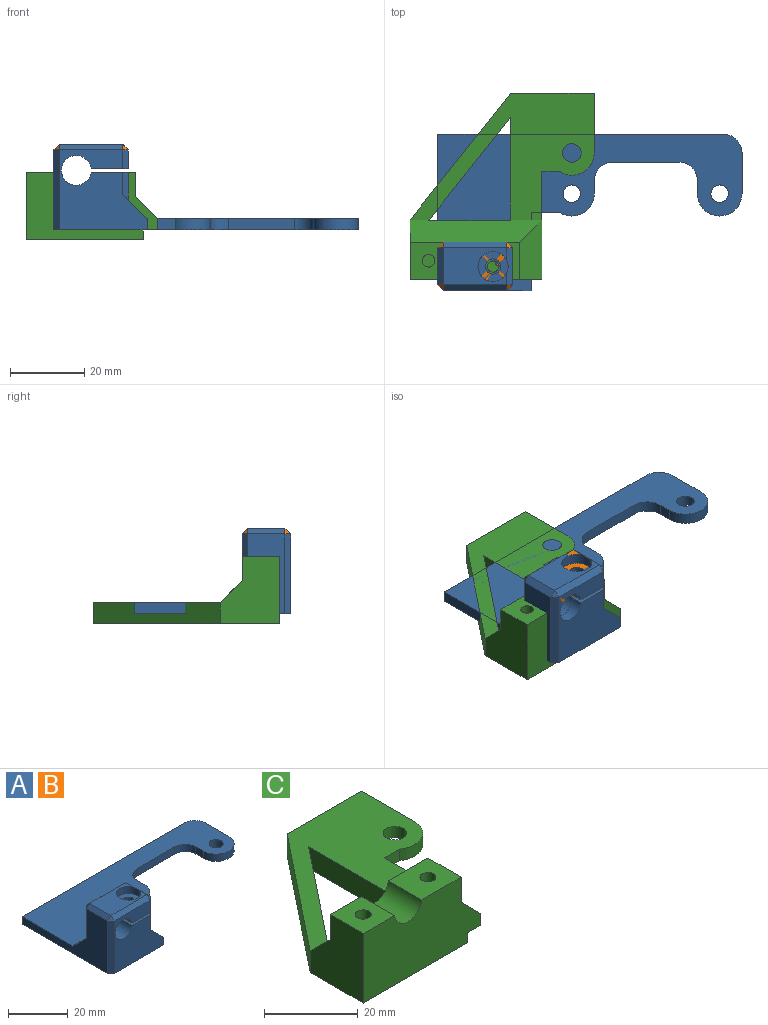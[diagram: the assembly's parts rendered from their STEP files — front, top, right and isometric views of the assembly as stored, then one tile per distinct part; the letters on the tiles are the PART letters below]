
ASSEMBLY  parts=3 mates=1
PART A: 46 faces, bbox 81.8x42x23 mm
  f0: plane 23.53x21.5mm, normal (0,-1,0), area 347.4mm2, adj f16,f18,f19,f22,f24,f25,f26,f37
  f1: plane 10x5mm, normal (1,0,0), area 50mm2, adj f25,f31,f36,f37
  f2: plane 10x7.5mm, normal (1,0,0), area 75mm2, adj f22,f26,f43,f44
  f3: plane 7.56x3mm, normal (0,-1,0), area 22.7mm2, adj f4,f16,f18,f19
  f4: cylinder r=6mm len=9.41mm, axis (0,0,-1), area 39.2mm2, adj f3,f5,f18,f19
  f5: plane 3.5x3mm, normal (1,0,0), area 10.5mm2, adj f4,f6,f18,f19
  f6: cylinder r=5mm len=5mm, axis (0,0,-1), area 23.6mm2, adj f5,f7,f18,f19
  f7: plane 17.75x3mm, normal (0,-1,0), area 53.2mm2, adj f6,f8,f18,f19
  f8: cylinder r=5mm len=5mm, axis (0,0,-1), area 23.6mm2, adj f7,f9,f18,f19
  f9: plane 3.5x3mm, normal (-1,0,0), area 10.5mm2, adj f8,f10,f18,f19
  f10: cylinder r=6mm len=12mm, axis (0,0,-1), area 56.5mm2, adj f9,f11,f18,f19
  f11: plane 11x3mm, normal (1,0,0), area 33mm2, adj f10,f12,f18,f19
  f12: cylinder r=5mm len=5mm, axis (0,0,-1), area 23.6mm2, adj f11,f13,f18,f19
  f13: plane 76.75x3mm, normal (0,1,0), area 230.3mm2, adj f12,f14,f18,f19
  f14: plane 40.54x21.5mm, normal (-1,0,0), area 327.7mm2, adj f13,f18,f19,f23,f32,f38,f39
  f15: cylinder r=2.35mm len=4.7mm, axis (0,0,-1), area 44.3mm2, adj f18,f19
  f16: plane 21.11x3mm, normal (1,0,0), area 63.3mm2, adj f0,f3,f18,f19
  f17: cylinder r=2.35mm len=4.7mm, axis (0,0,-1), area 44.3mm2, adj f18,f19
  f18: plane 81.75x42.04mm, normal (0,0,1), area 1385.9mm2, adj f0,f3,f4,f5,f6,f7,f8,f9
  f19: plane 81.75x42.04mm, normal (0,0,-1), area 1834.8mm2, adj f0,f3,f4,f5,f6,f7,f8,f9
  f20: plane 17x13.5mm, normal (0,1,0), area 170.7mm2, adj f23,f24,f25,f26,f31,f32,f33,f44
  f21: plane 17x10mm, normal (0,0,1), area 119.3mm2, adj f27,f33,f36,f39,f42
  f22: plane 18x6.5mm, normal (0.71,0,0.71), area 112mm2, adj f0,f2,f18,f23,f43,f44
  f23: plane 25x6.5mm, normal (0,0.71,0.71), area 161.5mm2, adj f14,f18,f20,f22,f32,f44
  f24: cylinder r=4mm len=13mm, axis (0,1,0), area 313.7mm2, adj f0,f20,f25,f26
  f25: plane 13x10.03mm, normal (0,0,-1), area 115mm2, adj f0,f1,f20,f24,f31,f37,f45
  f26: plane 13x10.03mm, normal (0,0,1), area 121.1mm2, adj f0,f2,f20,f24,f29,f43,f44
  f27: cylinder r=4.05mm len=8.1mm, axis (0,0,1), area 75.5mm2, adj f21,f28,f36
  f28: plane 8.1x8.1mm, normal (0,0,1), area 38.3mm2, adj f27,f45
  f29: cylinder r=1.5mm len=5.5mm, axis (0,0,1), area 51.8mm2, adj f26,f30
  f30: plane 3x3mm, normal (0,0,1), area 7.1mm2, adj f29
  f31: plane 5x1.5mm, normal (0.71,0.71,0), area 10.6mm2, adj f1,f20,f25,f34
  f32: plane 13.5x1.5mm, normal (-0.71,0.71,0), area 27mm2, adj f14,f20,f23,f35
  f33: plane 17x1.5mm, normal (0,0.71,0.71), area 36.1mm2, adj f20,f21,f34,f35
  f34: plane 1.5x1.5mm, normal (0.58,0.58,0.58), area 1.9mm2, adj f31,f33,f36
  f35: plane 1.5x1.5mm, normal (-0.58,0.58,0.58), area 1.9mm2, adj f32,f33,f39
  f36: plane 10x1.5mm, normal (0.71,0,0.71), area 20.1mm2, adj f1,f21,f27,f34,f40
  f37: plane 5x1.5mm, normal (0.71,-0.71,0), area 10.6mm2, adj f0,f1,f25,f40
  f38: plane 21.5x1.5mm, normal (-0.71,-0.71,0), area 45.6mm2, adj f0,f14,f19,f41
  f39: plane 10x1.5mm, normal (-0.71,0,0.71), area 21.2mm2, adj f14,f21,f35,f41
  f40: plane 1.5x1.5mm, normal (0.58,-0.58,0.58), area 1.9mm2, adj f36,f37,f42
  f41: plane 1.5x1.5mm, normal (-0.58,-0.58,0.58), area 1.9mm2, adj f38,f39,f42
  f42: plane 17x1.5mm, normal (0,-0.71,0.71), area 36.1mm2, adj f0,f21,f40,f41
  f43: plane 7.5x1.5mm, normal (0.71,-0.71,0), area 14.3mm2, adj f0,f2,f22,f26
  f44: plane 7.5x1.5mm, normal (0.71,0.71,0), area 15.1mm2, adj f2,f20,f22,f23,f26
  f45: cylinder r=2.05mm len=4.1mm, axis (0,0,1), area 45.1mm2, adj f25,f28
PART B: same geometry as A
PART C: 44 faces, bbox 49.5x50x18.1 mm
  f0: plane 8.5x7.8mm, normal (0,0,-1), area 33.2mm2, adj f2,f34,f35
  f1: plane 27.69x5.75mm, normal (-1,0,0), area 155.1mm2, adj f5,f8,f19,f32,f33
  f2: plane 7.8x2.6mm, normal (-1,0,0), area 20.3mm2, adj f0,f19,f34,f35
  f3: plane 22.46x5.6mm, normal (0,1,0), area 79mm2, adj f5,f9,f11,f18,f19,f22
  f4: plane 35.47x18.1mm, normal (0,-1,0), area 552.7mm2, adj f5,f7,f9,f10,f12,f16,f17,f18
  f5: plane 50x49.52mm, normal (0,0,1), area 721.3mm2, adj f1,f3,f4,f8,f11,f12,f13,f14
  f6: plane 29.52x6.55mm, normal (0,1,0), area 171mm2, adj f7,f8,f10,f16,f17,f21
  f7: plane 10x9.45mm, normal (0,0,1), area 85.4mm2, adj f4,f6,f16,f21,f26
  f8: plane 35.47x5.95mm, normal (0,0.71,0.71), area 268.9mm2, adj f1,f5,f6,f20,f21,f23,f32,f33
  f9: plane 50x18mm, normal (0,0,-1), area 473.3mm2, adj f3,f4,f11,f12,f13,f14,f15,f18
  f10: plane 10x6.55mm, normal (1,0,0), area 65.5mm2, adj f4,f6,f17,f20
  f11: plane 16x3mm, normal (1,0,0), area 48mm2, adj f3,f5,f9,f15
  f12: plane 29.07x3mm, normal (1,0,0), area 87.2mm2, adj f4,f5,f9,f13
  f13: plane 4.63x3mm, normal (0,-1,0), area 13.9mm2, adj f5,f9,f12,f15
  f14: cylinder r=2.5mm len=5mm, axis (0,0,-1), area 47.1mm2, adj f5,f9
  f15: cylinder r=6mm len=9.41mm, axis (0,0,-1), area 39.2mm2, adj f5,f9,f11,f13
  f16: cylinder r=4.1mm len=10mm, axis (0,1,0), area 118.8mm2, adj f4,f6,f7,f17
  f17: plane 11.93x10mm, normal (0,0,1), area 110.2mm2, adj f4,f6,f10,f16,f24
  f18: plane 50x2.6mm, normal (1,0,0), area 130mm2, adj f3,f4,f9,f19
  f19: plane 50x31.52mm, normal (0,0,-1), area 677.9mm2, adj f1,f2,f3,f4,f18,f21,f22,f23
  f20: plane 15.95x5.95mm, normal (0.71,0,0.71), area 109.2mm2, adj f4,f5,f8,f10
  f21: plane 18.1x15.95mm, normal (-1,0,0), area 232mm2, adj f4,f6,f7,f8,f19,f23
  f22: plane 34.05x27.06mm, normal (-0.78,0.62,0), area 243.6mm2, adj f3,f5,f19,f23
  f23: plane 5.6x0mm, normal (0,1,0), area 0mm2, adj f8,f19,f21,f22
  f24: cylinder r=1.7mm len=10.5mm, axis (0,0,1), area 112.2mm2, adj f17,f25
  f25: plane 3.4x3.4mm, normal (0,0,1), area 9.1mm2, adj f24
  f26: cylinder r=1.7mm len=10.5mm, axis (0,0,1), area 112.2mm2, adj f7,f27
  f27: plane 3.4x3.4mm, normal (0,0,1), area 9.1mm2, adj f26
  f28: plane 17x2.6mm, normal (0,-1,0), area 44.2mm2, adj f19,f29,f40,f41
  f29: plane 8.5x3.9mm, normal (0.42,0.91,0), area 24.3mm2, adj f19,f28,f40,f41
  f30: plane 8.5x3.9mm, normal (-0.42,-0.91,0), area 24.3mm2, adj f19,f31,f38,f43
  f31: plane 8.5x3.9mm, normal (0.42,-0.91,0), area 24.3mm2, adj f19,f30,f38,f43
  f32: plane 27.69x22mm, normal (0.78,-0.62,0), area 198.1mm2, adj f1,f5,f8,f19,f33
  f33: plane 22x5.75mm, normal (0,1,0), area 126.4mm2, adj f1,f8,f19,f32
  f34: plane 8.5x3.9mm, normal (0.42,-0.91,0), area 24.3mm2, adj f0,f2,f19,f35
  f35: plane 8.5x3.9mm, normal (0.42,0.91,0), area 24.3mm2, adj f0,f2,f19,f34
  f36: plane 8.5x3.9mm, normal (-0.42,-0.91,0), area 24.3mm2, adj f19,f37,f39,f42
  f37: plane 7.8x2.6mm, normal (1,0,0), area 20.3mm2, adj f19,f36,f39,f42
  f38: plane 17x2.6mm, normal (0,1,0), area 44.2mm2, adj f19,f30,f31,f43
  f39: plane 8.5x3.9mm, normal (-0.42,0.91,0), area 24.3mm2, adj f19,f36,f37,f42
  f40: plane 8.5x3.9mm, normal (-0.42,0.91,0), area 24.3mm2, adj f19,f28,f29,f41
  f41: plane 17x3.9mm, normal (0,0,-1), area 33.2mm2, adj f28,f29,f40
  f42: plane 8.5x7.8mm, normal (0,0,-1), area 33.2mm2, adj f36,f37,f39
  f43: plane 17x3.9mm, normal (0,0,-1), area 33.2mm2, adj f30,f31,f38
PLACE A t=(57.91,-14.32,27.28)mm
PLACE B t=(57.91,-14.32,27.28)mm
PLACE C t=(47.21,62.2,27.28)mm
MATE fastened C.f16 <-> B.f24  axis (0,1,0) through (-73.75,-4.61,43.28)mm
